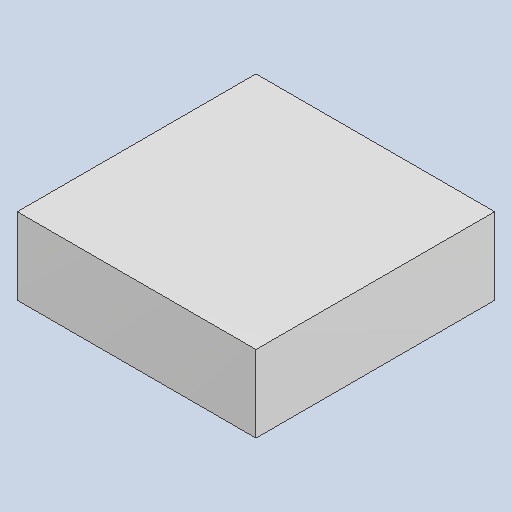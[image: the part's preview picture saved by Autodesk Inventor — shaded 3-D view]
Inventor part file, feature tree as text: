
AUTODESK INVENTOR PART (.ipt)
format: ipt  version: 2023.4 (Build 274418000, 418)  size: 79,872 bytes
history: native  units: mm
features: extrude x1
ambient origin geometry x8: Origin, YZ Plane, XZ Plane, XY Plane, X Axis, Y Axis, Z Axis, Center Point
bodies: Solid1 (feature_tree)
feature tree (1):
  extrude  "Extruded_11"  [1 undecoded]
note: 1 required parameter value undecoded (feature->parameter linkage not recoverable at this tier; creation-order binding heuristic only, values carry confidence <= 0.55)
